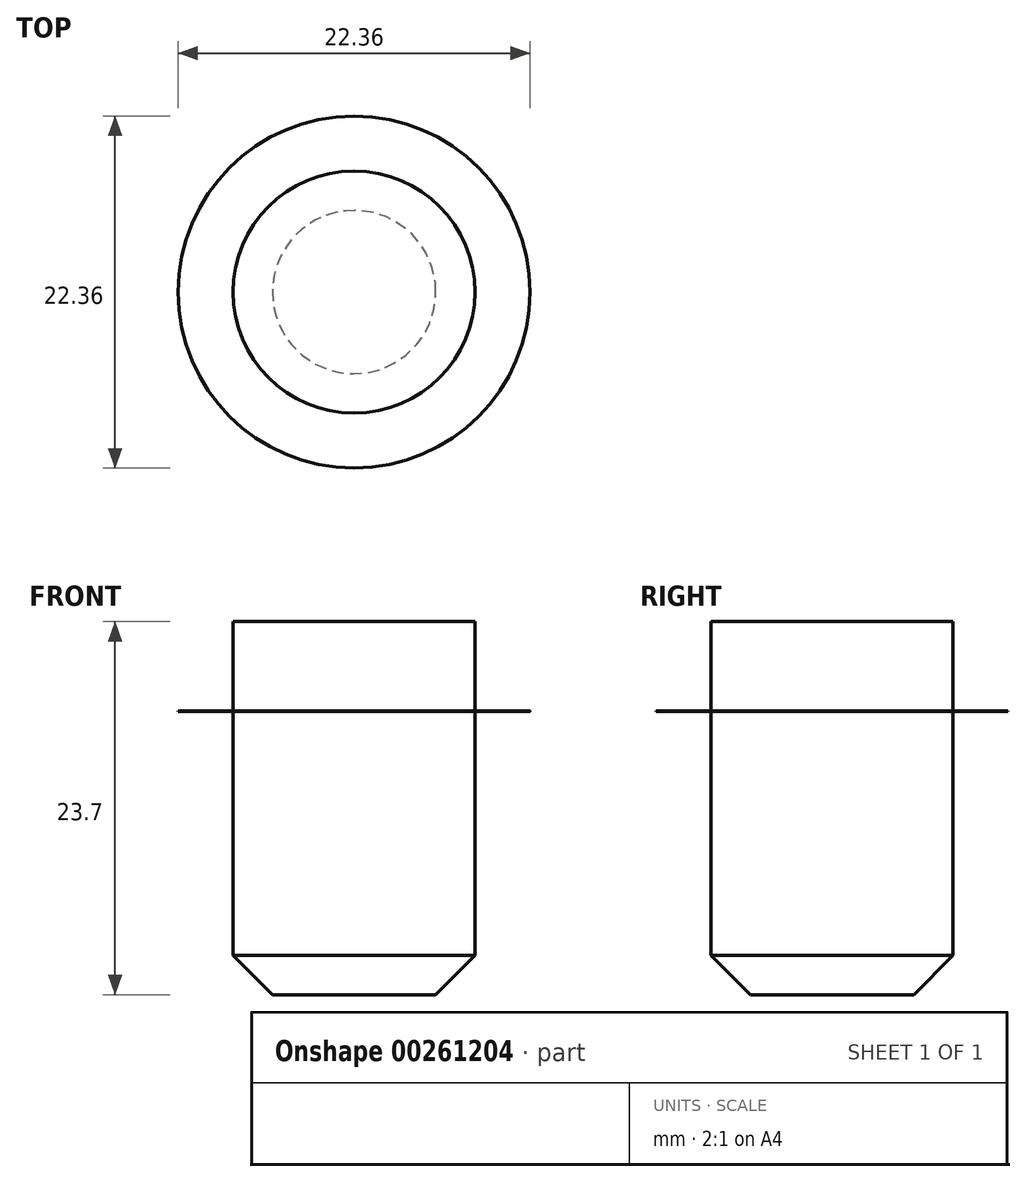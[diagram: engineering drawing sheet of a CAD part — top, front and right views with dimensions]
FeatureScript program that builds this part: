
annotation { "Feature Type Name" : "Feature", "Feature Type Description" : "" }
export const myFeature = defineFeature(function(context is Context, id is Id, definition is map)
    precondition{}
    {
        {
            var Q0;
            Q0=qCreatedBy(makeId("Top.planeOp"),FACE);
            var sketch = newSketch(context, id + "F0", { "sketchPlane" : qUnion([Q0])});
            skCircle(sketch, "E0", {"center": v(0, 0) * mm, "radius": 11.18 * mm});
            skCircle(sketch, "E1", {"center": v(0, 0) * mm, "radius": 7.68 * mm});
            skSolve(sketch);
        }
        {
            var Q0;
            Q0=makeQuery(id+"F0.imprint","IMPRINT",FACE,{"disambiguationData":[TD([[makeQuery(id+"F0.imprint","IMPRINT",EDGE,{"derivedFrom":sQuery(id+"F0.wireOp",EDGE,"E0")}),1.0]])]});
            extrude(context, id + "F1", {"entities" : qUnion([Q0]), "depth" : 1 / 50.8 * mm});
        }
        {
            var Q0;
            Q0=makeQuery(id+"F0.imprint","IMPRINT",FACE,{"disambiguationData":[TD([[makeQuery(id+"F0.imprint","IMPRINT",EDGE,{"derivedFrom":sQuery(id+"F0.wireOp",EDGE,"E1")}),1.0]])]});
            extrude(context, id + "F2", {"entities" : qUnion([Q0]), "oppositeDirection" : true, "depth" : 18 * mm});
        }
        {
            var Q0;
            Q0=makeQuery(id+"F0.imprint","IMPRINT",FACE,{"disambiguationData":[TD([[makeQuery(id+"F0.imprint","IMPRINT",EDGE,{"derivedFrom":sQuery(id+"F0.wireOp",EDGE,"E1")}),1.0]])]});
            extrude(context, id + "F3", {"entities" : qUnion([Q0]), "operationType" : NewBodyOperationType.ADD, "depth" : 5.7 * mm});
        }
        {
            var Q0;
            Q0=makeQuery(id+"F2.opExtrude","CAP_EDGE",EDGE,{"disambiguationData":[OSD([sQuery(id+"F0.wireOp",EDGE,"E1")])],"isStart":false});
            chamfer(context, id + "F4", {"entities" : qUnion([Q0]), "width" : 2.5 * mm, "tangentPropagation" : true});
        }
    });
